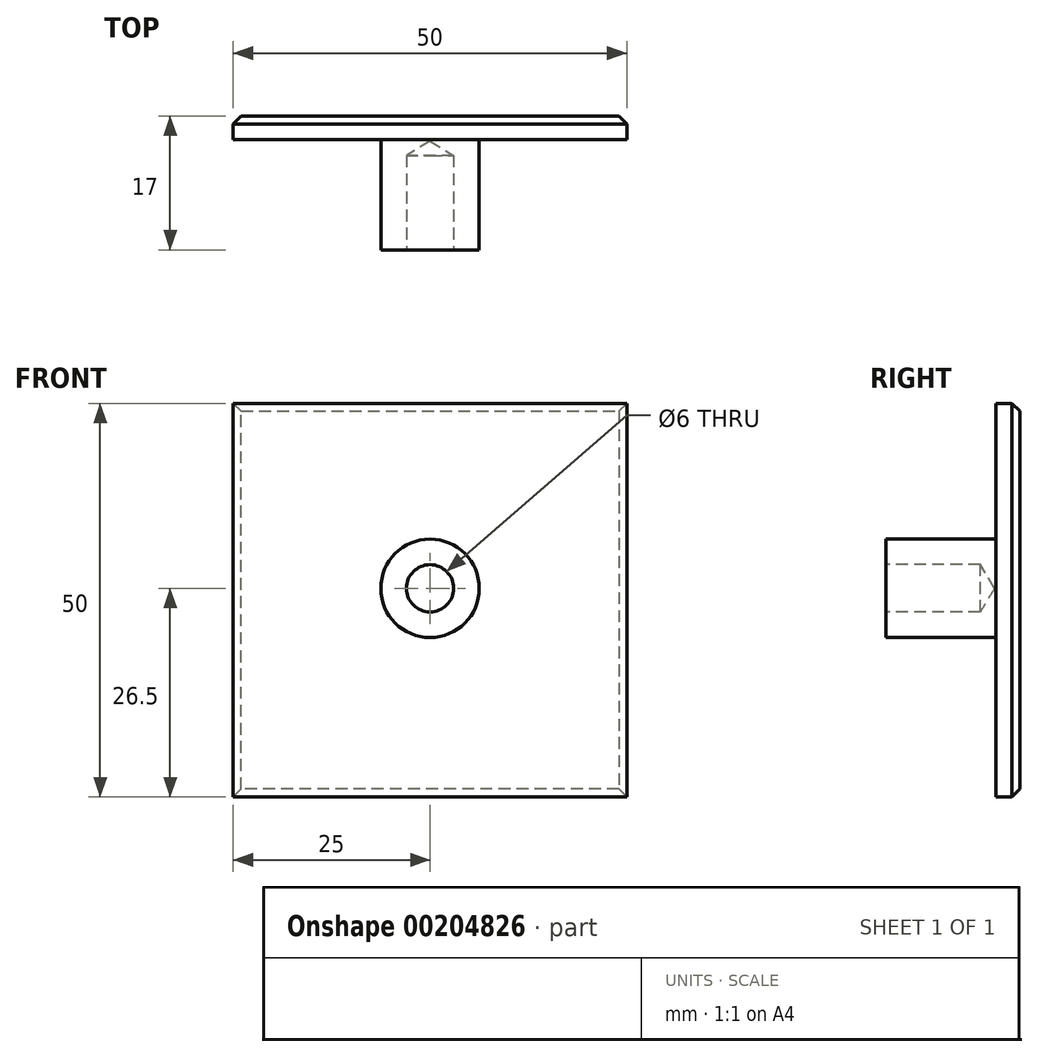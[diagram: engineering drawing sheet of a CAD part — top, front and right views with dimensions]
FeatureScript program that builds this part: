
annotation { "Feature Type Name" : "Feature", "Feature Type Description" : "" }
export const myFeature = defineFeature(function(context is Context, id is Id, definition is map)
    precondition{}
    {
        {
            var Q0;
            Q0=qCreatedBy(makeId("Front.planeOp"),FACE);
            var sketch = newSketch(context, id + "F0", { "sketchPlane" : qUnion([Q0])});
            skLineSegment(sketch, "E0.bottom", {"start": v(0, 0) * mm, "end": v(50, 0) * mm});
            skLineSegment(sketch, "E0.top", {"start": v(0, 50) * mm, "end": v(50, 50) * mm});
            skLineSegment(sketch, "E0.left", {"start": v(0, 0) * mm, "end": v(0, 50) * mm});
            skLineSegment(sketch, "E0.right", {"start": v(50, 0) * mm, "end": v(50, 50) * mm});
            skSolve(sketch);
        }
        {
            var Q0;
            Q0=makeQuery(id+"F0.imprint","IMPRINT",FACE,{"disambiguationData":[TD([[makeQuery(id+"F0.imprint","IMPRINT",EDGE,{"derivedFrom":sQuery(id+"F0.wireOp",EDGE,"E0.bottom")}),1.0]])]});
            var sketch = newSketch(context, id + "F1", { "sketchPlane" : qUnion([Q0])});
            skCircle(sketch, "E1", {"center": v(25, 26.5) * mm, "radius": 6.25 * mm});
            skSolve(sketch);
        }
        {
            var Q0;
            Q0=makeQuery(id+"F1.imprint","IMPRINT",FACE,{"disambiguationData":[TD([[makeQuery(id+"F1.imprint","IMPRINT",EDGE,{"derivedFrom":sQuery(id+"F1.wireOp",EDGE,"E1")}),1.0]])]});
            extrude(context, id + "F2", {"entities" : qUnion([Q0]), "depth" : 14 * mm});
        }
        {
            var Q0;
            Q0=makeQuery(id+"F0.imprint","IMPRINT",FACE,{"disambiguationData":[TD([[makeQuery(id+"F0.imprint","IMPRINT",EDGE,{"derivedFrom":sQuery(id+"F0.wireOp",EDGE,"E0.bottom")}),1.0]])]});
            extrude(context, id + "F3", {"entities" : qUnion([Q0]), "operationType" : NewBodyOperationType.ADD, "oppositeDirection" : true, "depth" : 3 * mm});
        }
        {
            var Q0;
            Q0=makeQuery(id+"F2.opExtrude","CAP_FACE",FACE,{"disambiguationData":[OSD([sQuery(id+"F1.wireOp",EDGE,"E1")])],"isStart":false});
            var sketch = newSketch(context, id + "F4", { "sketchPlane" : qUnion([Q0])});
            skCircle(sketch, "E2", {"center": v(25, 26.5) * mm, "radius": 3 * mm});
            skSolve(sketch);
        }
        {
            var Q0;
            Q0=sQuery(id+"F4.wireOp",VERTEX,"E2.center");
            var Q1;
            Q1=makeQuery(id+"F2.opExtrude","SWEPT_BODY",BODY,{"disambiguationData":[OSD([sQuery(id+"F1.wireOp",EDGE,"E1")])]});
            hole(context, id + "F5", {"style" : HoleStyle.SIMPLE, "endStyle" : HoleEndStyle.BLIND, "holeDiameter" : 6 * mm, "holeDepth" : 12 * mm, "locations" : qUnion([Q0]), "scope" : qUnion([Q1])});
        }
        {
            var Q0;
            Q0=makeQuery(id+"F3.opExtrude","CAP_EDGE",EDGE,{"disambiguationData":[OSD([sQuery(id+"F0.wireOp",EDGE,"E0.top")])],"isStart":false});
            var Q1;
            Q1=makeQuery(id+"F3.opExtrude","CAP_EDGE",EDGE,{"disambiguationData":[OSD([sQuery(id+"F0.wireOp",EDGE,"E0.right")])],"isStart":false});
            var Q2;
            Q2=makeQuery(id+"F3.opExtrude","CAP_FACE",FACE,{"disambiguationData":[OSD([sQuery(id+"F0.wireOp",EDGE,"E0.bottom"),sQuery(id+"F0.wireOp",EDGE,"E0.top"),sQuery(id+"F0.wireOp",EDGE,"E0.left"),sQuery(id+"F0.wireOp",EDGE,"E0.right")])],"isStart":false});
            chamfer(context, id + "F6", {"entities" : qUnion([Q0, Q1, Q2]), "width" : 1 * mm, "tangentPropagation" : true});
        }
    });
